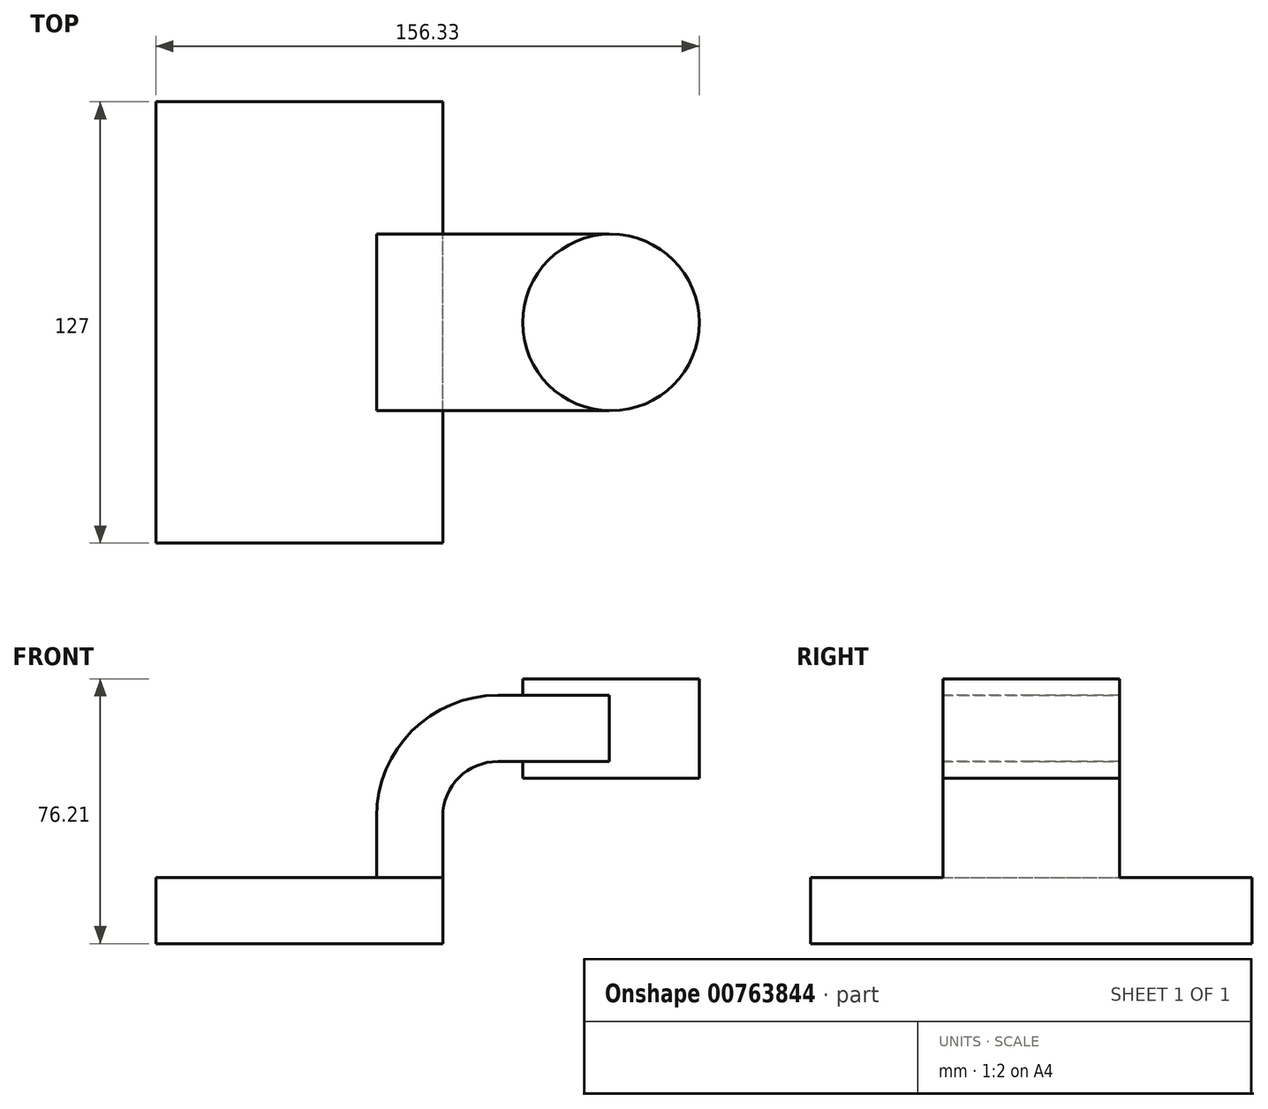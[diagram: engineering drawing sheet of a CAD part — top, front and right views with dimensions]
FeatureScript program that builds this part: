
annotation { "Feature Type Name" : "Feature", "Feature Type Description" : "" }
export const myFeature = defineFeature(function(context is Context, id is Id, definition is map)
    precondition{}
    {
        {
            var Q0;
            Q0=qCreatedBy(makeId("Front.planeOp"),FACE);
            var sketch = newSketch(context, id + "F0", { "sketchPlane" : qUnion([Q0])});
            skLineSegment(sketch, "E0.bottom", {"start": v(-41.27, -9.53) * mm, "end": v(41.28, -9.53) * mm});
            skLineSegment(sketch, "E0.top", {"start": v(-41.28, 9.53) * mm, "end": v(41.28, 9.53) * mm});
            skLineSegment(sketch, "E0.left", {"start": v(-41.28, -9.53) * mm, "end": v(-41.28, 9.53) * mm});
            skLineSegment(sketch, "E0.right", {"start": v(41.28, -9.53) * mm, "end": v(41.28, 9.53) * mm});
            skPoint(sketch, "E0.middle", {"position": v(0, 0) * mm});
            skLineSegment(sketch, "E1.bottom", {"start": v(64.25, 66.67) * mm, "end": v(115.05, 66.67) * mm});
            skLineSegment(sketch, "E1.top", {"start": v(64.25, 38.1) * mm, "end": v(115.05, 38.1) * mm});
            skLineSegment(sketch, "E1.left", {"start": v(64.25, 66.67) * mm, "end": v(64.25, 38.1) * mm});
            skLineSegment(sketch, "E1.right", {"start": v(115.05, 66.67) * mm, "end": v(115.05, 38.1) * mm});
            skPoint(sketch, "E1.middle", {"position": v(89.65, 52.39) * mm});
            skLineSegment(sketch, "E2", {"start": v(41.28, 9.52) * mm, "end": v(41.28, 27) * mm});
            skPoint(sketch, "E3.endSnap0", {"position": v(64.25, 52.39) * mm});
            skArc(sketch, "E4", {"start": v(41.27, 27) * mm, "mid": v(45.92, 38.23) * mm, "end": v(57.15, 42.88) * mm});
            skLineSegment(sketch, "E5", {"start": v(57.15, 42.88) * mm, "end": v(89.65, 42.88) * mm});
            skLineSegment(sketch, "E6.0", {"start": v(57.15, 61.93) * mm, "end": v(89.65, 61.93) * mm});
            skArc(sketch, "E6.1", {"start": v(22.23, 27) * mm, "mid": v(32.45, 51.7) * mm, "end": v(57.15, 61.93) * mm});
            skLineSegment(sketch, "E6.2", {"start": v(22.22, 9.52) * mm, "end": v(22.22, 27) * mm});
            skLineSegment(sketch, "E7", {"start": v(89.65, 38.1) * mm, "end": v(89.65, 66.67) * mm});
            skPoint(sketch, "E7.startSnap0", {"position": v(89.65, 38.1) * mm});
            skFitSpline(sketch, "E8", {"points": [v(-41.28, 9.53) * mm, v(57.15, 61.93) * mm], "startDerivative": vector(42.03, 84.37) * mm, "endDerivative": vector(114.05, -54.86) * mm});
            skSolve(sketch);
        }
        {
            var Q0;
            Q0=makeQuery(id+"F0.imprint","IMPRINT",FACE,{"disambiguationData":[TD([[makeQuery(id+"F0.imprint","IMPRINT",EDGE,{"derivedFrom":sQuery(id+"F0.wireOp",EDGE,"E0.bottom")}),1.0]])]});
            extrude(context, id + "F1", {"entities" : qUnion([Q0]), "endBound" : BoundingType.SYMMETRIC, "depth" : 127 * mm, "offsetDistance" : 25.4 * mm});
        }
        {
            var Q0;
            {var subQ1=sQuery(id+"F0.wireOp",EDGE,"E2");Q0=makeQuery(id+"F0.imprint","IMPRINT",FACE,{"disambiguationData":[TD([[makeQuery(id+"F0.imprint","IMPRINT",EDGE,{"derivedFrom":subQ1}),1.0]])]});}
            var Q1;
            {var subQ0=sQuery(id+"F0.wireOp",EDGE,"E6.0");var subQ1=sQuery(id+"F0.wireOp",EDGE,"E1.left");var subQ2=makeQuery(id+"F0.imprint","INTERSECT",VERTEX,{"derivedFrom":[subQ1,subQ0]});Q1=makeQuery(id+"F0.imprint","IMPRINT",FACE,{"disambiguationData":[TD([[makeQuery(id+"F0.imprint","IMPRINT",EDGE,{"disambiguationData":[TD([[subQ2,-1.0]])],"derivedFrom":subQ1}),1.0]])]});}
            extrude(context, id + "F2", {"entities" : qUnion([Q0, Q1]), "operationType" : NewBodyOperationType.ADD, "endBound" : BoundingType.SYMMETRIC, "depth" : 50.8 * mm, "offsetDistance" : 25.4 * mm});
        }
        {
            var Q0;
            Q0=makeQuery(id+"F0.imprint","IMPRINT",FACE,{"disambiguationData":[TD([[makeQuery(id+"F0.imprint","IMPRINT",EDGE,{"derivedFrom":sQuery(id+"F0.wireOp",EDGE,"E6.1")}),1.0]])]});
            extrude(context, id + "F3", {"entities" : qUnion([Q0]), "operationType" : NewBodyOperationType.ADD, "endBound" : BoundingType.SYMMETRIC, "depth" : 15.88 * mm, "offsetDistance" : 25.4 * mm});
        }
        {
            var Q0;
            {var subQ0=sQuery(id+"F0.wireOp",EDGE,"E1.right");Q0=makeQuery(id+"F0.imprint","IMPRINT",FACE,{"disambiguationData":[TD([[makeQuery(id+"F0.imprint","IMPRINT",EDGE,{"derivedFrom":subQ0}),-1.0]])]});}
            var Q1;
            Q1=sQuery(id+"F0.wireOp",EDGE,"E7");
            revolve(context, id + "F4", {"operationType" : NewBodyOperationType.ADD, "surfaceOperationType" : NewSurfaceOperationType.NEW, "entities" : qUnion([Q0]), "axis" : qUnion([Q1]), "revolveType" : RevolveType.FULL});
        }
    });
